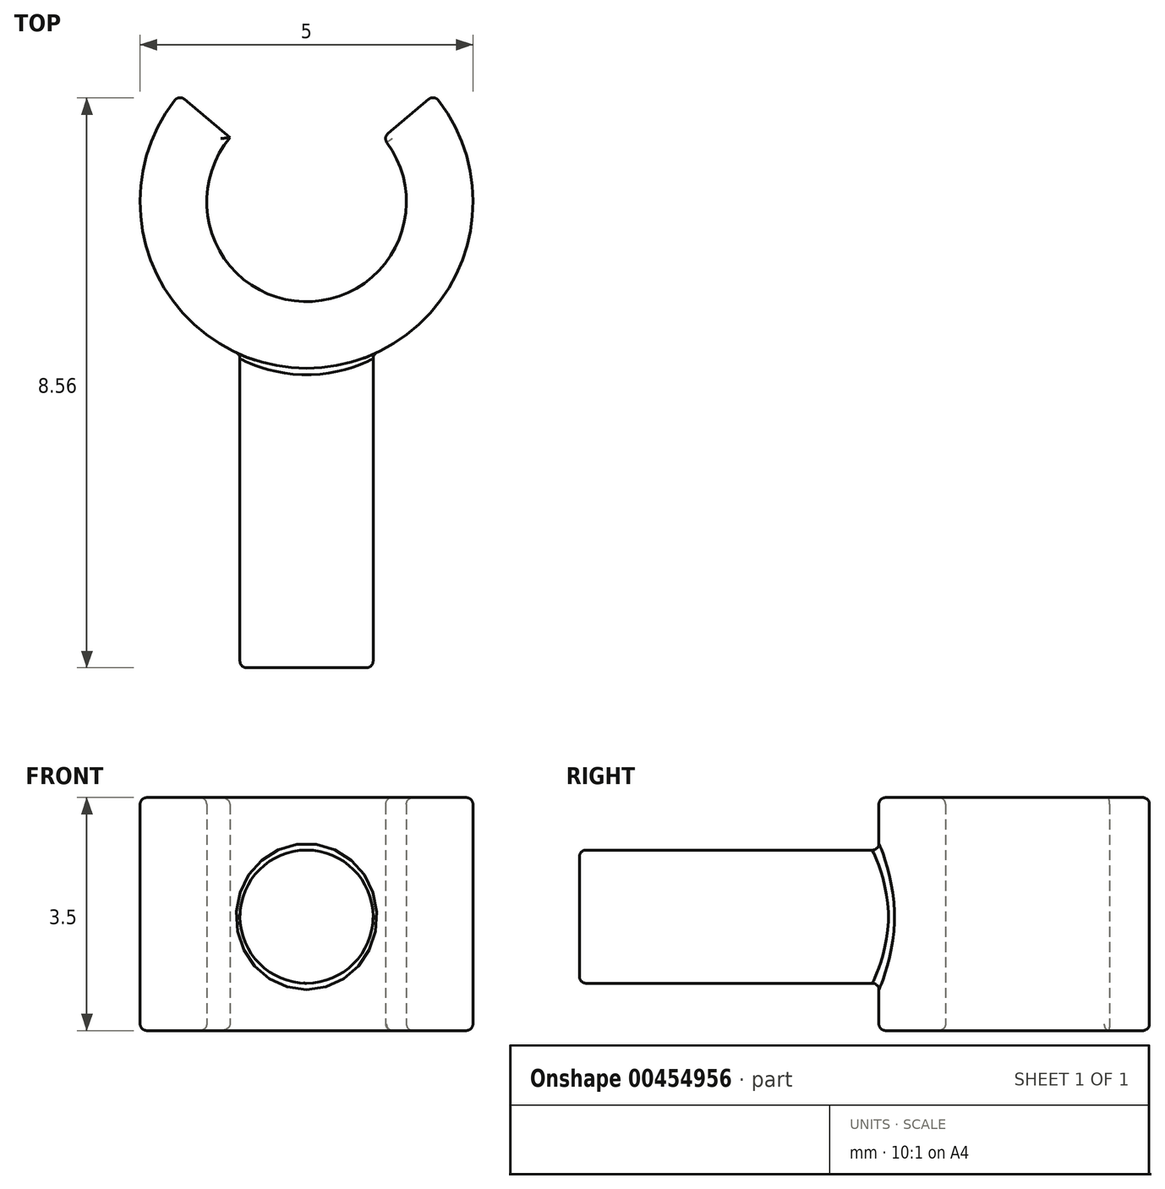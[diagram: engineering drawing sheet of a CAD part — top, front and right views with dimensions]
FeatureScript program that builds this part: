
annotation { "Feature Type Name" : "Feature", "Feature Type Description" : "" }
export const myFeature = defineFeature(function(context is Context, id is Id, definition is map)
    precondition{}
    {
        {
            var Q0;
            Q0=qCreatedBy(makeId("Top.planeOp"),FACE);
            var sketch = newSketch(context, id + "F0", { "sketchPlane" : qUnion([Q0])});
            skArc(sketch, "E0", {"start": v(-1.15, 0.96) * mm, "mid": v(0, -1.5) * mm, "end": v(1.15, 0.96) * mm});
            skArc(sketch, "E1", {"start": v(-1.92, 1.6) * mm, "mid": v(0, -2.5) * mm, "end": v(1.92, 1.6) * mm});
            skLineSegment(sketch, "E2", {"start": v(-1.15, 0.96) * mm, "end": v(-1.92, 1.6) * mm});
            skLineSegment(sketch, "E3", {"start": v(1.15, 0.96) * mm, "end": v(1.92, 1.6) * mm});
            skSolve(sketch);
        }
        {
            var Q0;
            Q0 = qSketchRegion(id + "F0", true);
            extrude(context, id + "F1", {"entities" : qUnion([Q0]), "depth" : 3.5 * mm});
        }
        {
            var Q0;
            Q0=qCreatedBy(makeId("Front.planeOp"),FACE);
            cPlane(context, id + "F2", {"entities" : qUnion([Q0]), "cplaneType" : CPlaneType.OFFSET, "offset" : 7 * mm, "width" : 150 * mm, "height" : 150 * mm});
        }
        {
            var Q0;
            Q0=qCreatedBy(id+"F2.planeOp",FACE);
            var sketch = newSketch(context, id + "F3", { "sketchPlane" : qUnion([Q0])});
            skCircle(sketch, "E4", {"center": v(0, 1.71) * mm, "radius": 1 * mm});
            skSolve(sketch);
        }
        {
            var Q0;
            Q0 = qSketchRegion(id + "F3", true);
            var Q1;
            Q1=makeQuery(id+"F1.opExtrude","SWEPT_FACE",FACE,{"disambiguationData":[OSD([sQuery(id+"F0.wireOp",EDGE,"E1")])]});
            extrude(context, id + "F4", {"entities" : qUnion([Q0]), "operationType" : NewBodyOperationType.ADD, "endBound" : BoundingType.UP_TO_SURFACE, "oppositeDirection" : true, "endBoundEntityFace" : qUnion([Q1]), "depth" : 25 * mm});
        }
        {
            var Q0;
            Q0=makeQuery(id+"F4.opExtrude","SWEPT_FACE",FACE,{"disambiguationData":[OSD([sQuery(id+"F3.wireOp",EDGE,"E4")])]});
            var Q1;
            Q1=makeQuery(id+"F1.opExtrude","SWEPT_FACE",FACE,{"disambiguationData":[OSD([sQuery(id+"F0.wireOp",EDGE,"E3")])]});
            var Q2;
            Q2=makeQuery(id+"F1.opExtrude","CAP_FACE",FACE,{"disambiguationData":[OSD([sQuery(id+"F0.wireOp",EDGE,"E0"),sQuery(id+"F0.wireOp",EDGE,"E1"),sQuery(id+"F0.wireOp",EDGE,"E2"),sQuery(id+"F0.wireOp",EDGE,"E3")])],"isStart":true});
            var Q3;
            Q3=makeQuery(id+"F1.opExtrude","SWEPT_FACE",FACE,{"disambiguationData":[OSD([sQuery(id+"F0.wireOp",EDGE,"E1")])]});
            var Q4;
            Q4=makeQuery(id+"F1.opExtrude","CAP_FACE",FACE,{"disambiguationData":[OSD([sQuery(id+"F0.wireOp",EDGE,"E0"),sQuery(id+"F0.wireOp",EDGE,"E1"),sQuery(id+"F0.wireOp",EDGE,"E2"),sQuery(id+"F0.wireOp",EDGE,"E3")])],"isStart":false});
            fillet(context, id + "F5", {"entities" : qUnion([Q0, Q1, Q2, Q3, Q4]), "radius" : 0.1 * mm, "tangentPropagation" : true, "allowEdgeOverflow" : false});
        }
    });
